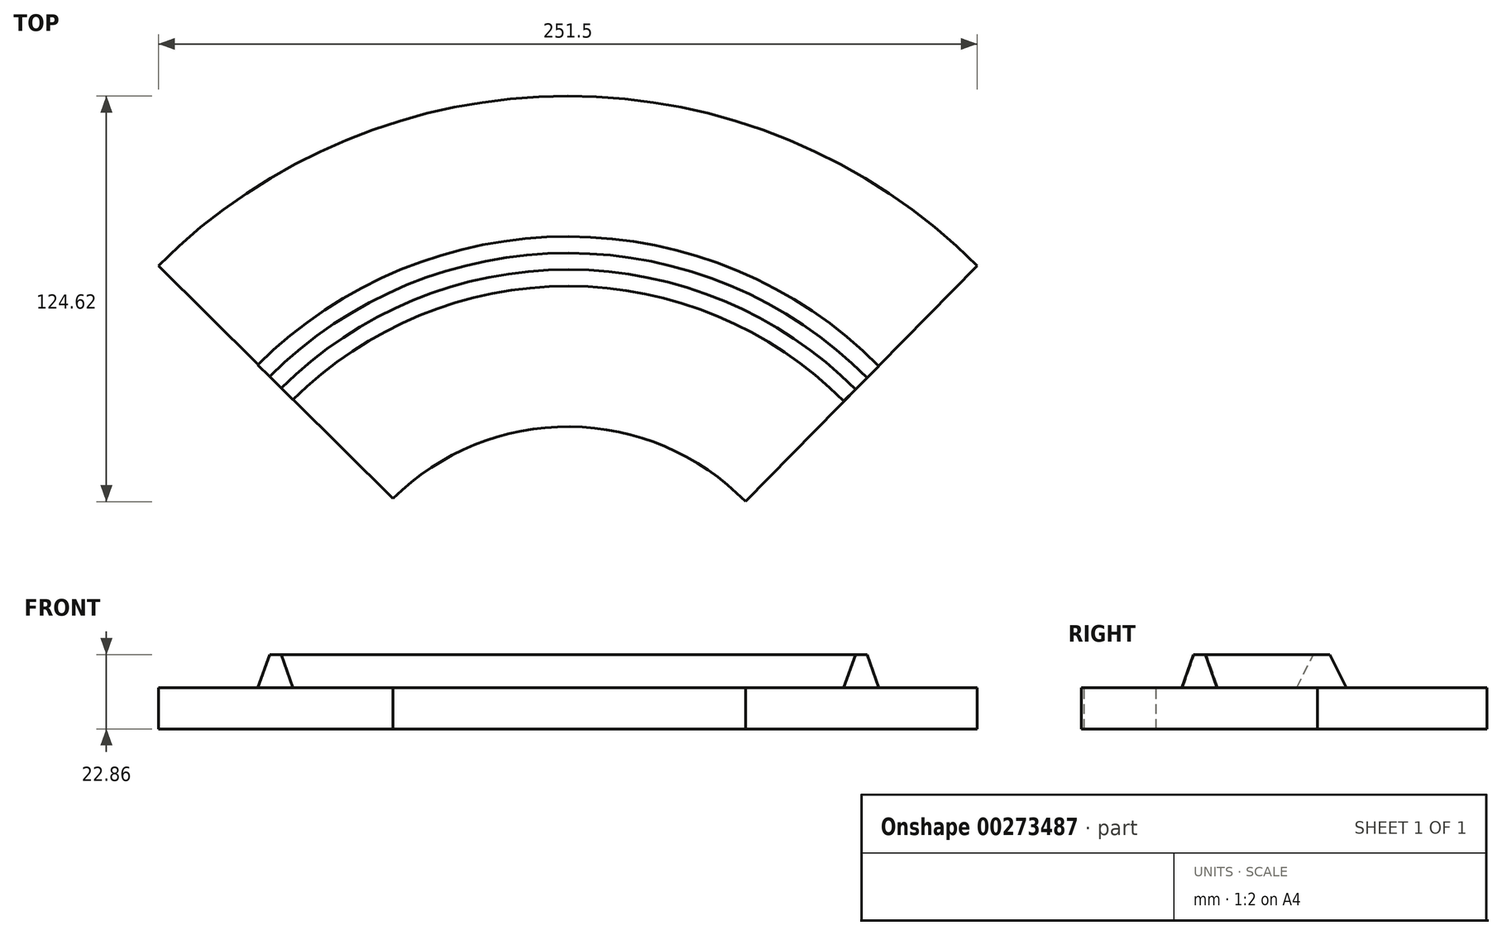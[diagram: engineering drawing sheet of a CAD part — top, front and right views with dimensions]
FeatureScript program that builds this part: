
annotation { "Feature Type Name" : "Feature", "Feature Type Description" : "" }
export const myFeature = defineFeature(function(context is Context, id is Id, definition is map)
    precondition{}
    {
        {
            var Q0;
            Q0=qCreatedBy(makeId("Top.planeOp"),FACE);
            var sketch = newSketch(context, id + "F0", { "sketchPlane" : qUnion([Q0])});
            skArc(sketch, "E0", {"start": v(54.58, 53.17) * mm, "mid": v(0.65, 76.2) * mm, "end": v(-53.66, 54.1) * mm});
            skLineSegment(sketch, "E1", {"start": v(0, 0) * mm, "end": v(-53.66, 54.1) * mm, "construction": true});
            skLineSegment(sketch, "E2", {"start": v(0, 0) * mm, "end": v(54.58, 53.17) * mm, "construction": true});
            skArc(sketch, "E3", {"start": v(125.75, 125.68) * mm, "mid": v(0, 177.79) * mm, "end": v(-125.75, 125.68) * mm});
            skArc(sketch, "E4.0", {"start": v(90.16, 89.43) * mm, "mid": v(0.26, 127) * mm, "end": v(-89.8, 89.8) * mm});
            skLineSegment(sketch, "E5", {"start": v(90.16, 89.43) * mm, "end": v(134.98, 44.24) * mm, "construction": true});
            skLineSegment(sketch, "E6", {"start": v(54.58, 53.17) * mm, "end": v(125.75, 125.68) * mm});
            skLineSegment(sketch, "E7", {"start": v(-125.75, 125.68) * mm, "end": v(-53.66, 54.1) * mm});
            skSolve(sketch);
        }
        {
            var Q0;
            Q0=sQuery(id+"F0.wireOp",VERTEX,"E4.0.start");
            var Q1;
            Q1=sQuery(id+"F0.wireOp",EDGE,"E5");
            cPlane(context, id + "F1", {"entities" : qUnion([Q0, Q1]), "cplaneType" : CPlaneType.LINE_POINT, "offset" : 25.4 * mm, "width" : 152.4 * mm, "height" : 152.4 * mm});
        }
        {
            var Q0;
            Q0=qCreatedBy(id+"F1.planeOp",FACE);
            var sketch = newSketch(context, id + "F2", { "sketchPlane" : qUnion([Q0])});
            skLineSegment(sketch, "E8", {"start": v(127, 0) * mm, "end": v(127, 48.42) * mm, "construction": true});
            skLineSegment(sketch, "E9", {"start": v(119.38, 0) * mm, "end": v(124.46, 10.16) * mm});
            skLineSegment(sketch, "E10", {"start": v(124.46, 10.16) * mm, "end": v(127, 10.16) * mm});
            skLineSegment(sketch, "E11.MirrorCS", {"start": v(129.54, 10.16) * mm, "end": v(127, 10.16) * mm});
            skLineSegment(sketch, "E12.MirrorCS", {"start": v(134.62, 0) * mm, "end": v(129.54, 10.16) * mm});
            skLineSegment(sketch, "E13", {"start": v(119.38, 0) * mm, "end": v(127, 0) * mm});
            skLineSegment(sketch, "E14.MirrorCS", {"start": v(134.62, 0) * mm, "end": v(127, 0) * mm});
            skSolve(sketch);
        }
        {
            var Q0;
            Q0=makeQuery(id+"F2.imprint","IMPRINT",FACE,{"disambiguationData":[TD([[makeQuery(id+"F2.imprint","IMPRINT",EDGE,{"derivedFrom":sQuery(id+"F2.wireOp",EDGE,"E9")}),-1.0]])]});
            var Q1;
            Q1=sQuery(id+"F0.wireOp",EDGE,"E4.0");
            sweep(context, id + "F3", {"profiles" : qUnion([Q0]), "path" : qUnion([Q1])});
        }
        {
            var Q0;
            Q0 = qSketchRegion(id + "F0", true);
            extrude(context, id + "F4", {"entities" : qUnion([Q0]), "oppositeDirection" : true, "depth" : 12.7 * mm});
        }
    });
